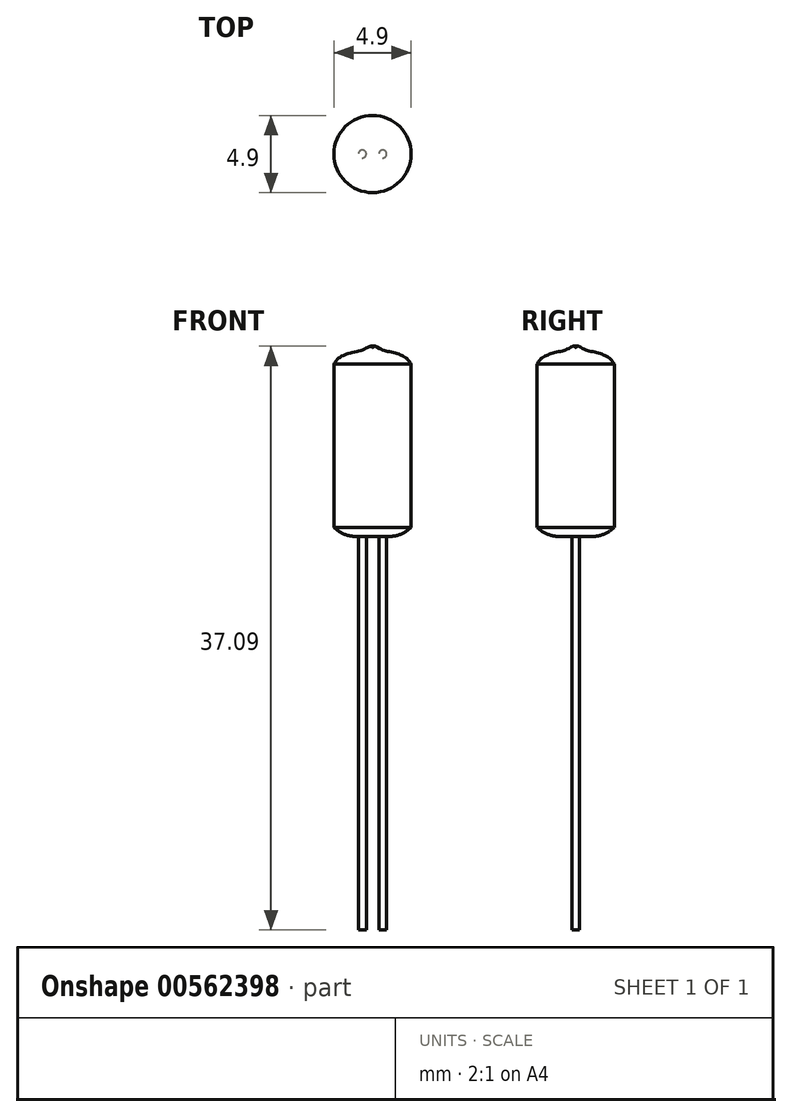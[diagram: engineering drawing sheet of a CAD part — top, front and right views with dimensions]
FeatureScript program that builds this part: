
annotation { "Feature Type Name" : "Feature", "Feature Type Description" : "" }
export const myFeature = defineFeature(function(context is Context, id is Id, definition is map)
    precondition{}
    {
        {
            var Q0;
            Q0=qCreatedBy(makeId("Front.planeOp"),FACE);
            var sketch = newSketch(context, id + "F0", { "sketchPlane" : qUnion([Q0])});
            skLineSegment(sketch, "E0.bottom", {"start": v(0, 0) * mm, "end": v(-1.04, 0) * mm});
            skLineSegment(sketch, "E0.left", {"start": v(0, 0) * mm, "end": v(0, 12) * mm});
            skPoint(sketch, "E1.visualSharp", {"position": v(-2.45, 0) * mm});
            skArc(sketch, "E1.filletArc", {"start": v(-2.45, 0.58) * mm, "mid": v(-1.8, 0.15) * mm, "end": v(-1.04, 0) * mm});
            skLineSegment(sketch, "E2", {"start": v(-2.45, 0.58) * mm, "end": v(-2.45, 10.94) * mm});
            skFitSpline(sketch, "E3", {"points": [v(-2.45, 10.94) * mm, v(-2.42, 11) * mm, v(-2.28, 11.19) * mm, v(-2.18, 11.3) * mm, v(-2.13, 11.33) * mm, v(-2.01, 11.41) * mm, v(-1.86, 11.5) * mm, v(-1.8, 11.52) * mm, v(-1.64, 11.58) * mm, v(-1.59, 11.6) * mm, v(-1.36, 11.66) * mm, v(-1.29, 11.7) * mm, v(-1, 11.75) * mm, v(-0.93, 11.76) * mm, v(-0.7, 11.83) * mm, v(-0.6, 11.86) * mm, v(-0.44, 11.94) * mm, v(-0.37, 11.98) * mm, v(-0.18, 12.08) * mm, v(-0.12, 12.08) * mm, v(0, 12) * mm], "startDerivative": vector(0.76, 1.4) * mm, "endDerivative": vector(2.57, -2) * mm});
            skSolve(sketch);
        }
        {
            var Q0;
            Q0 = qSketchRegion(id + "F0", true);
            var Q1;
            Q1=sQuery(id+"F0.wireOp",EDGE,"E0.left");
            revolve(context, id + "F1", {"entities" : qUnion([Q0]), "axis" : qUnion([Q1]), "revolveType" : RevolveType.FULL});
        }
        {
            var Q0;
            Q0=makeQuery(id+"F1.opRevolve","SWEPT_FACE",FACE,{"disambiguationData":[OSD([sQuery(id+"F0.wireOp",EDGE,"E0.bottom")])]});
            var sketch = newSketch(context, id + "F2", { "sketchPlane" : qUnion([Q0])});
            skCircle(sketch, "E4", {"center": v(0.65, 0) * mm, "radius": 0.25 * mm});
            skCircle(sketch, "E5.1.0", {"center": v(-0.65, 0) * mm, "radius": 0.25 * mm});
            skPoint(sketch, "E5.center", {"position": v(0, 0) * mm});
            skSolve(sketch);
        }
        {
            var Q0;
            Q0 = qSketchRegion(id + "F2", true);
            extrude(context, id + "F3", {"entities" : qUnion([Q0]), "operationType" : NewBodyOperationType.ADD, "depth" : 25 * mm, "offsetDistance" : 25 * mm});
        }
    });
